# Revit family: Toilet-Elongated-DXV-Eurocube-3966_Series
name_source: partatom
category: Plumbing Fixtures
revit_build: Autodesk Revit 2014 (Build: 20130308_1515(x64)
units: mm (PartAtom-declared; Revit-internal decimal feet)

## types (3) — shared parameters
ADA Compliant = No
Assembly Code = D2010110
Bowl Shape = Elongated Bowl
CW Connection = Yes
CWFU = 3
Cold Water Connection Diameter = 1/2"
Cold Water Connection Height = 8"
Cold Water Connection Radius = 1/4"
Cold Water Connection Width = 3"
Default Elevation = 0"
Description = Eurocube Two-Piece Elongated Dual Flush Toilet
Finish = Vitreous China-Grohe-000-Alpine White
Flush Rate = 1.0 gpf - 1.28 gpf (3.8 Lpf - 4.8 Lpf)
HW Connection = No
Height = 30 13/16"
Installation Type = Floor Mounted
Length = 29 3/8"
Manufacturer = Grohe
Material = Vitreous China-Grohe-000-Alpine White
Price = Prices may vary. Please consult Manufacturer Rep for most up-to-date price list.
URL = https://www.grohe.us
Vent Connection = No
WFU = 3
Warranty Documentation Link = https://www.grohe.us
Waste Connection = Yes
Waste Connection Diameter = 2 1/8"
Waste Connection Radius = 1 1/16"
Width = 14 15/16"
zero-valued in all types: HWFU

## per-type parameters (varying)
| type | Left Handle | Right Handle | Top Flush |
| 39661000 | No | No | Yes |
| 39662000 | Yes | No | No |
| 39663000 | No | Yes | No |

note: column(s) folded — value = type name in every type: Model

## geometry (parser evidence)
native form markers: Sweep x1
no freeform markers — native parametric forms only
